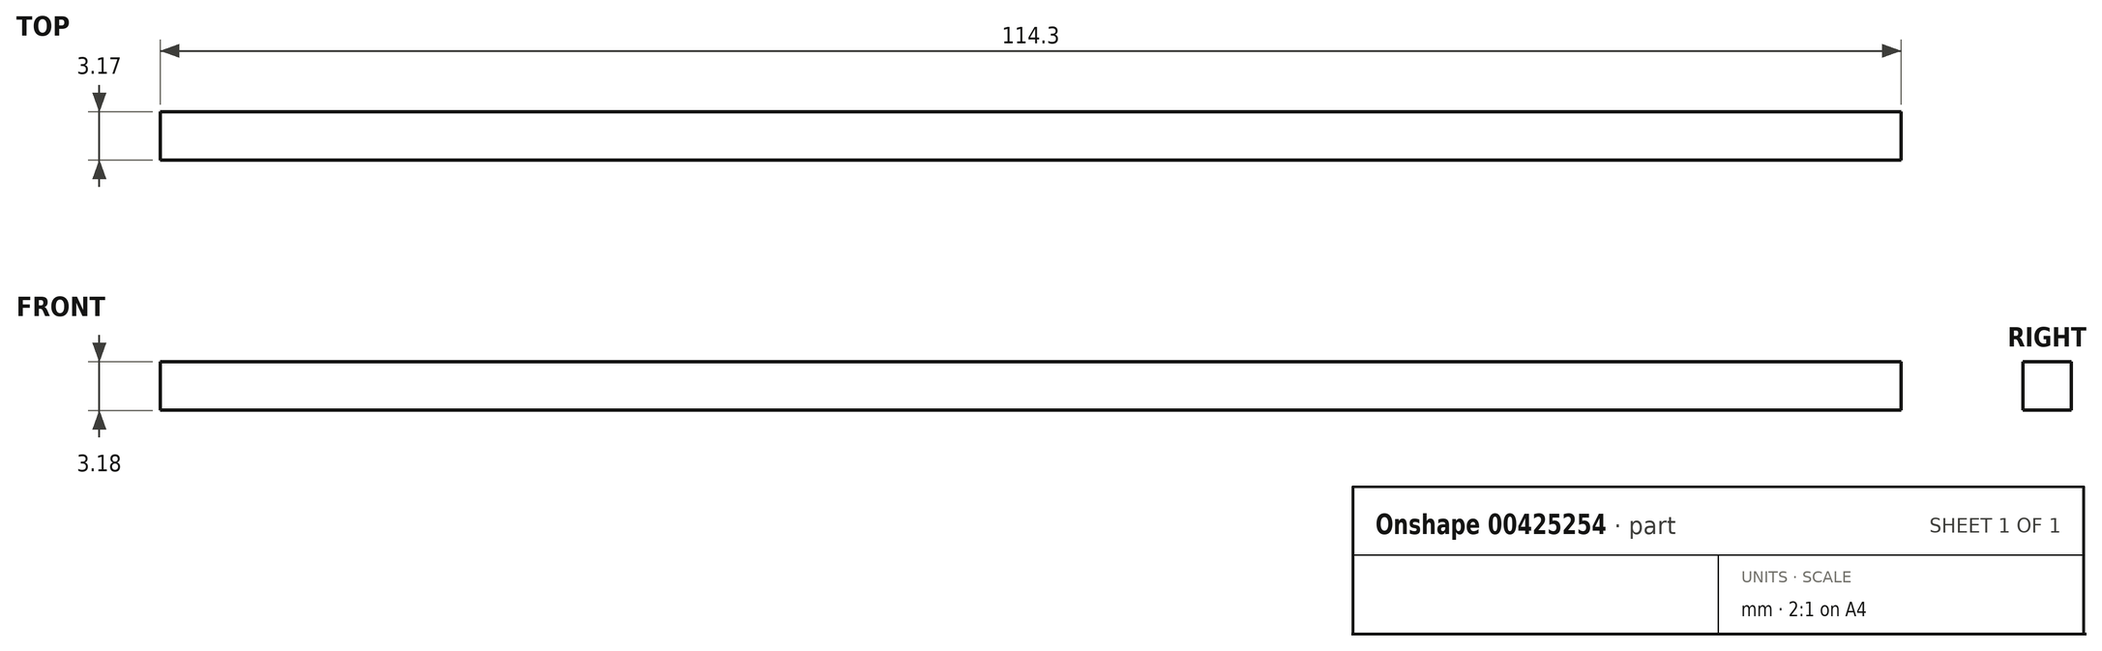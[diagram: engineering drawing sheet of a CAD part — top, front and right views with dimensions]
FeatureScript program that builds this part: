
annotation { "Feature Type Name" : "Feature", "Feature Type Description" : "" }
export const myFeature = defineFeature(function(context is Context, id is Id, definition is map)
    precondition{}
    {
        {
            var Q0;
            Q0=qCreatedBy(makeId("Front.planeOp"),FACE);
            var sketch = newSketch(context, id + "F0", { "sketchPlane" : qUnion([Q0])});
            skLineSegment(sketch, "E0.bottom", {"start": v(-62, 41.83) * mm, "end": v(52.3, 41.83) * mm});
            skLineSegment(sketch, "E0.top", {"start": v(-62, 38.65) * mm, "end": v(52.3, 38.65) * mm});
            skLineSegment(sketch, "E0.left", {"start": v(-62, 41.83) * mm, "end": v(-62, 38.65) * mm});
            skLineSegment(sketch, "E0.right", {"start": v(52.3, 41.83) * mm, "end": v(52.3, 38.65) * mm});
            skSolve(sketch);
        }
        {
            var Q0;
            Q0 = qSketchRegion(id + "F0", true);
            extrude(context, id + "F1", {"entities" : qUnion([Q0]), "depth" : 3.17 * mm});
        }
    });
